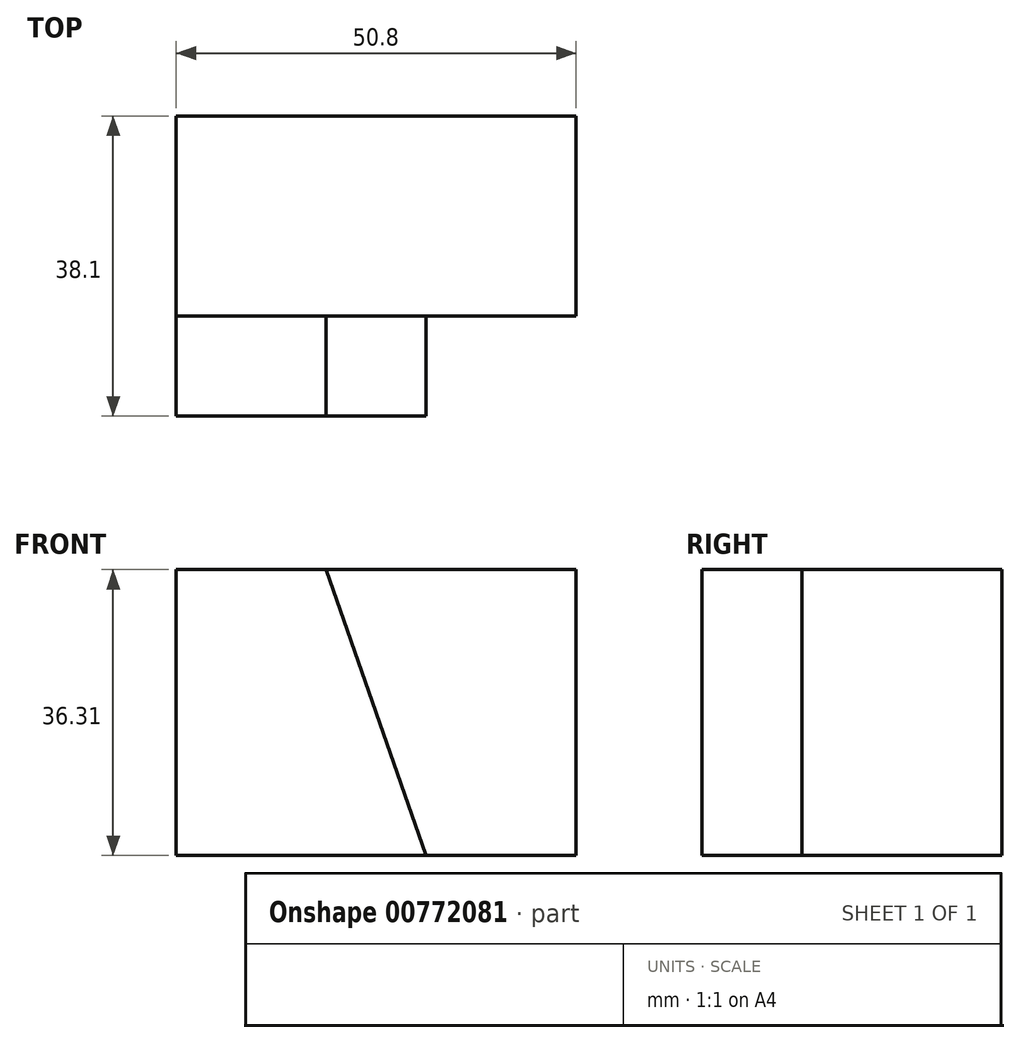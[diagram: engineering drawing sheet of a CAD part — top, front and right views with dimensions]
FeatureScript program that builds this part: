
annotation { "Feature Type Name" : "Feature", "Feature Type Description" : "" }
export const myFeature = defineFeature(function(context is Context, id is Id, definition is map)
    precondition{}
    {
        {
            var Q0;
            Q0=qCreatedBy(makeId("Front.planeOp"),FACE);
            var sketch = newSketch(context, id + "F0", { "sketchPlane" : qUnion([Q0])});
            skLineSegment(sketch, "E0", {"start": v(0, 0) * mm, "end": v(0, 36.31) * mm});
            skLineSegment(sketch, "E1", {"start": v(0, 36.31) * mm, "end": v(50.8, 36.31) * mm});
            skLineSegment(sketch, "E2", {"start": v(50.8, 36.31) * mm, "end": v(50.8, 0) * mm});
            skLineSegment(sketch, "E3", {"start": v(50.8, 0) * mm, "end": v(0, 0) * mm});
            skSolve(sketch);
        }
        {
            var Q0;
            Q0 = qSketchRegion(id + "F0", true);
            extrude(context, id + "F1", {"entities" : qUnion([Q0]), "depth" : 25.4 * mm, "offsetDistance" : 25.4 * mm});
        }
        {
            var Q0;
            Q0 = qSketchRegion(id + "F0", true);
            extrude(context, id + "F2", {"entities" : qUnion([Q0]), "depth" : 38.1 * mm, "offsetDistance" : 25.4 * mm});
        }
        {
            var Q0;
            Q0=makeQuery(id+"F2.opExtrude","CAP_FACE",FACE,{"disambiguationData":[OSD([sQuery(id+"F0.wireOp",EDGE,"E0"),sQuery(id+"F0.wireOp",EDGE,"E1"),sQuery(id+"F0.wireOp",EDGE,"E2"),sQuery(id+"F0.wireOp",EDGE,"E3")])],"isStart":false});
            var sketch = newSketch(context, id + "F3", { "sketchPlane" : qUnion([Q0])});
            skLineSegment(sketch, "E4", {"start": v(0, 36.31) * mm, "end": v(19.06, 36.31) * mm});
            skLineSegment(sketch, "E5", {"start": v(0, 0) * mm, "end": v(19.06, 0) * mm});
            skLineSegment(sketch, "E6", {"start": v(19.06, 0) * mm, "end": v(31.71, 0) * mm});
            skLineSegment(sketch, "E7", {"start": v(19.06, 36.31) * mm, "end": v(31.71, 0) * mm});
            skSolve(sketch);
        }
        {
            var Q0;
            {var subQ0=sQuery(id+"F3.wireOp",EDGE,"E7");Q0=makeQuery(id+"F3.imprint","IMPRINT",FACE,{"disambiguationData":[TD([[makeQuery(id+"F3.imprint","IMPRINT",EDGE,{"derivedFrom":subQ0}),1.0]])]});}
            extrude(context, id + "F4", {"entities" : qUnion([Q0]), "operationType" : NewBodyOperationType.REMOVE, "oppositeDirection" : true, "depth" : 12.7 * mm, "offsetDistance" : 25.4 * mm});
        }
    });
